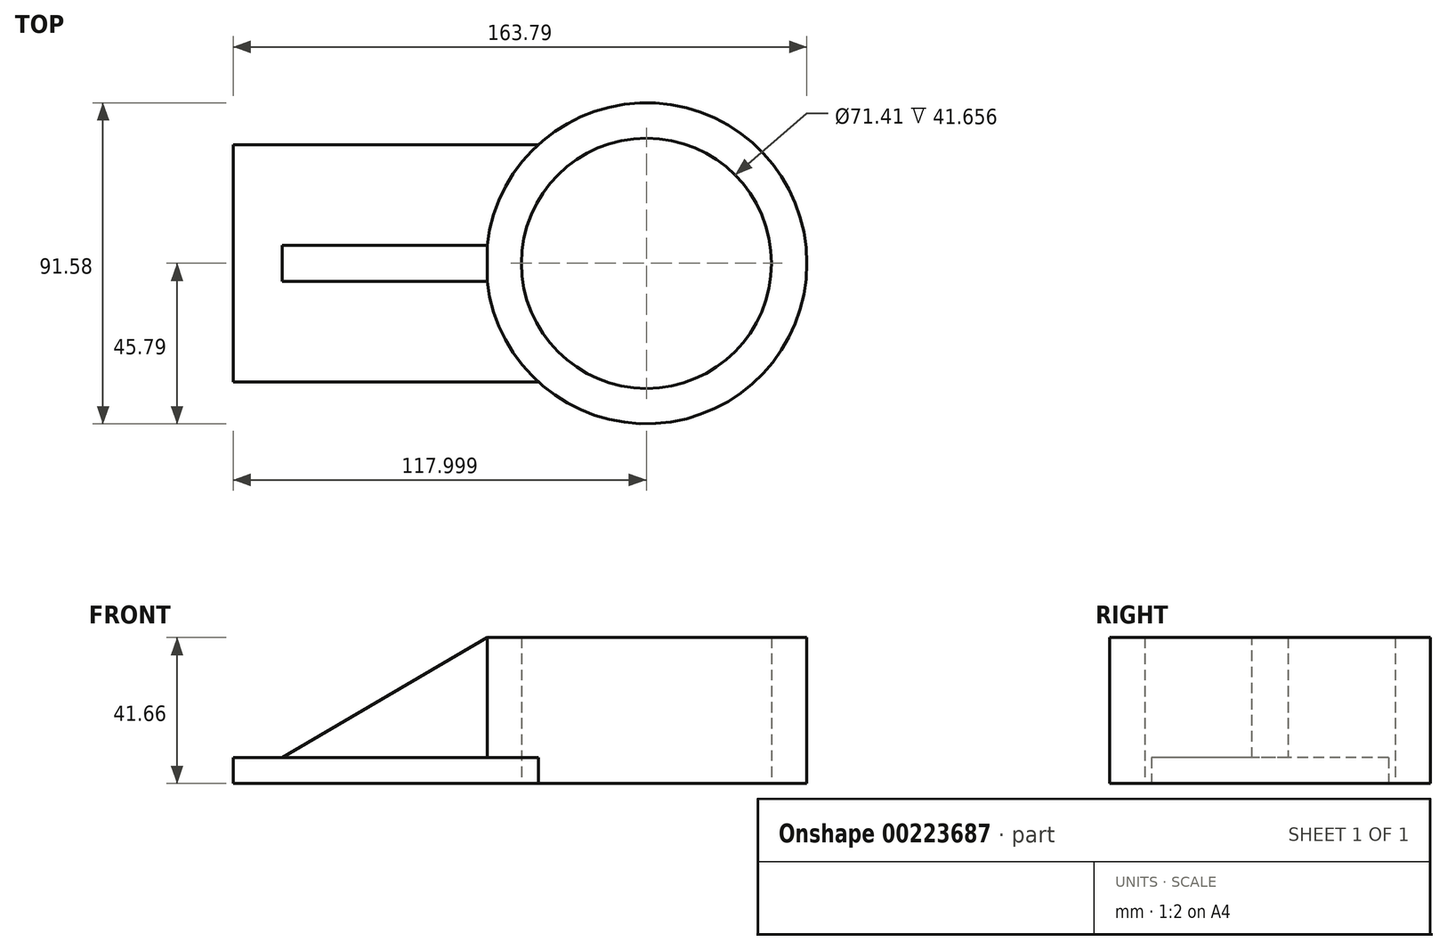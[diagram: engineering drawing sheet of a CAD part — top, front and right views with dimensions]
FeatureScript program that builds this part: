
annotation { "Feature Type Name" : "Feature", "Feature Type Description" : "" }
export const myFeature = defineFeature(function(context is Context, id is Id, definition is map)
    precondition{}
    {
        {
            var Q0;
            Q0=qCreatedBy(makeId("Top.planeOp"),FACE);
            var sketch = newSketch(context, id + "F0", { "sketchPlane" : qUnion([Q0])});
            skLineSegment(sketch, "E0.right", {"start": v(-59, 33.81) * mm, "end": v(-59, -33.81) * mm});
            skPoint(sketch, "E0.middle", {"position": v(0, 0) * mm});
            skCircle(sketch, "E1", {"center": v(59, 0) * mm, "radius": 45.8 * mm});
            skCircle(sketch, "E2", {"center": v(59, 0) * mm, "radius": 35.7 * mm});
            skLineSegment(sketch, "E3.trimOffspring", {"start": v(28.12, 33.81) * mm, "end": v(-59, 33.81) * mm});
            skPoint(sketch, "E4.orphan", {"position": v(59, 33.81) * mm});
            skLineSegment(sketch, "E5.trimOffspring", {"start": v(28.12, -33.81) * mm, "end": v(-59, -33.81) * mm});
            skPoint(sketch, "E0.top.start.orphan", {"position": v(59, -33.81) * mm});
            skSolve(sketch);
        }
        {
            var Q0;
            Q0=makeQuery(id+"F0.imprint","IMPRINT",FACE,{"disambiguationData":[TD([[makeQuery(id+"F0.imprint","IMPRINT",EDGE,{"derivedFrom":sQuery(id+"F0.wireOp",EDGE,"E0.right")}),1.0]])]});
            var Q1;
            Q1=makeQuery(id+"F0.imprint","IMPRINT",FACE,{"disambiguationData":[TD([[makeQuery(id+"F0.imprint","IMPRINT",EDGE,{"derivedFrom":sQuery(id+"F0.wireOp",EDGE,"E2")}),-1.0]])]});
            extrude(context, id + "F1", {"entities" : qUnion([Q0, Q1]), "depth" : 41.66 * mm});
        }
        {
            var Q0;
            Q0=makeQuery(id+"F1.opExtrude","CAP_FACE",FACE,{"disambiguationData":[OSD([sQuery(id+"F0.wireOp",EDGE,"E0.right"),sQuery(id+"F0.wireOp",EDGE,"E1"),sQuery(id+"F0.wireOp",EDGE,"E2"),sQuery(id+"F0.wireOp",EDGE,"E3.trimOffspring"),sQuery(id+"F0.wireOp",EDGE,"E5.trimOffspring")])],"isStart":false});
            var sketch = newSketch(context, id + "F2", { "sketchPlane" : qUnion([Q0])});
            skCircle(sketch, "E6", {"center": v(59, 0) * mm, "radius": 45.8 * mm});
            skLineSegment(sketch, "E7.bottom", {"start": v(-45, 5.15) * mm, "end": v(13.5, 5.15) * mm});
            skLineSegment(sketch, "E7.top", {"start": v(-45, -5.15) * mm, "end": v(13.5, -5.15) * mm});
            skLineSegment(sketch, "E7.left", {"start": v(-45, 5.15) * mm, "end": v(-45, -5.15) * mm});
            skPoint(sketch, "E7.middle", {"position": v(0, 0) * mm});
            skPoint(sketch, "E8.orphan", {"position": v(45, 5.15) * mm});
            skPoint(sketch, "E9.orphan", {"position": v(45, -5.15) * mm});
            skLineSegment(sketch, "E10", {"start": v(28.12, 33.81) * mm, "end": v(-59, 33.81) * mm});
            skLineSegment(sketch, "E11", {"start": v(-59, 33.81) * mm, "end": v(-59, -33.81) * mm});
            skLineSegment(sketch, "E12", {"start": v(-59, -33.81) * mm, "end": v(28.12, -33.81) * mm});
            skSolve(sketch);
        }
        {
            var Q0;
            Q0=makeQuery(id+"F2.imprint","IMPRINT",FACE,{"disambiguationData":[TD([[makeQuery(id+"F2.imprint","IMPRINT",EDGE,{"derivedFrom":makeQuery(id+"F1.opExtrude","CAP_EDGE",EDGE,{"disambiguationData":[OSD([sQuery(id+"F0.wireOp",EDGE,"E2")])],"isStart":false})}),1.0]])]});
            var Q1;
            {var subQ1=sQuery(id+"F2.wireOp",EDGE,"E7.bottom");Q1=makeQuery(id+"F2.imprint","IMPRINT",FACE,{"disambiguationData":[TD([[makeQuery(id+"F2.imprint","IMPRINT",EDGE,{"derivedFrom":subQ1}),1.0]])]});}
            extrude(context, id + "F3", {"entities" : qUnion([Q0, Q1]), "operationType" : NewBodyOperationType.REMOVE, "oppositeDirection" : true, "depth" : 34.3 * mm});
        }
        {
            var Q0;
            Q0=makeQuery(id+"F3.boolean.opBoolean","COPY",FACE,{"derivedFrom":makeQuery(id+"F3.opExtrude","SWEPT_FACE",FACE,{"disambiguationData":[OSD([sQuery(id+"F2.wireOp",EDGE,"E7.top")])]})});
            var sketch = newSketch(context, id + "F4", { "sketchPlane" : qUnion([Q0])});
            skLineSegment(sketch, "E13", {"start": v(13.5, 41.66) * mm, "end": v(-45, 7.37) * mm});
            skLineSegment(sketch, "E14", {"start": v(-45, 7.37) * mm, "end": v(13.5, 7.37) * mm});
            skLineSegment(sketch, "E15", {"start": v(13.5, 7.37) * mm, "end": v(13.5, 41.66) * mm});
            skSolve(sketch);
        }
        {
            var Q0;
            Q0=makeQuery(id+"F4.imprint","IMPRINT",FACE,{"disambiguationData":[TD([[makeQuery(id+"F4.imprint","IMPRINT",EDGE,{"derivedFrom":sQuery(id+"F4.wireOp",EDGE,"E13")}),-1.0]])]});
            extrude(context, id + "F5", {"entities" : qUnion([Q0]), "operationType" : NewBodyOperationType.REMOVE, "oppositeDirection" : true, "depth" : 25.4 * mm});
        }
    });
